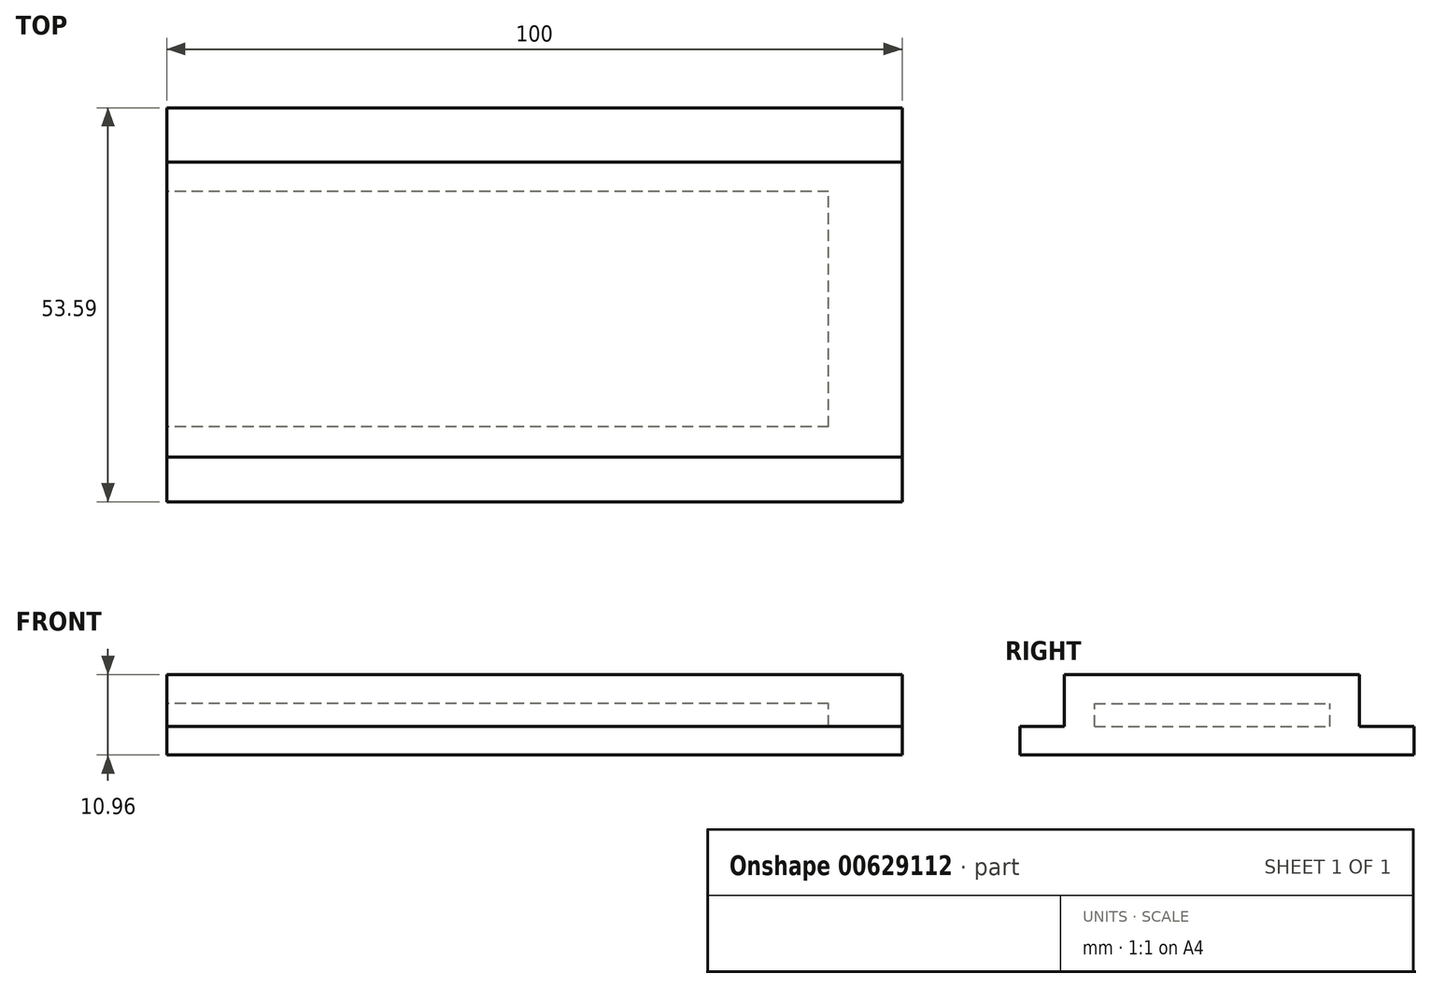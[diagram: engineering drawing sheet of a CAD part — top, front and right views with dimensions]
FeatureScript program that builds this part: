
annotation { "Feature Type Name" : "Feature", "Feature Type Description" : "" }
export const myFeature = defineFeature(function(context is Context, id is Id, definition is map)
    precondition{}
    {
        {
            var Q0;
            Q0=qCreatedBy(makeId("Right.planeOp"),FACE);
            var sketch = newSketch(context, id + "F0", { "sketchPlane" : qUnion([Q0])});
            skLineSegment(sketch, "E0", {"start": v(0, 0) * mm, "end": v(-24.54, 0) * mm});
            skLineSegment(sketch, "E1", {"start": v(-24.54, 0) * mm, "end": v(-24.54, 3.92) * mm});
            skLineSegment(sketch, "E2", {"start": v(-24.54, 3.92) * mm, "end": v(-18.5, 3.92) * mm});
            skLineSegment(sketch, "E3", {"start": v(-18.5, 3.92) * mm, "end": v(-18.5, 10.96) * mm});
            skLineSegment(sketch, "E4", {"start": v(-18.5, 10.96) * mm, "end": v(21.64, 10.96) * mm});
            skLineSegment(sketch, "E5", {"start": v(21.64, 10.96) * mm, "end": v(21.64, 3.92) * mm});
            skLineSegment(sketch, "E6", {"start": v(21.64, 3.92) * mm, "end": v(29.05, 3.92) * mm});
            skLineSegment(sketch, "E7", {"start": v(29.05, 3.92) * mm, "end": v(29.05, 0) * mm});
            skLineSegment(sketch, "E8", {"start": v(29.05, 0) * mm, "end": v(0, 0) * mm});
            skLineSegment(sketch, "E9.bottom", {"start": v(-14.37, 3.9) * mm, "end": v(17.63, 3.9) * mm});
            skLineSegment(sketch, "E9.top", {"start": v(-14.37, 7) * mm, "end": v(17.63, 7) * mm});
            skLineSegment(sketch, "E9.left", {"start": v(-14.37, 3.9) * mm, "end": v(-14.37, 7) * mm});
            skLineSegment(sketch, "E9.right", {"start": v(17.63, 3.9) * mm, "end": v(17.63, 7) * mm});
            skSolve(sketch);
        }
        {
            var Q0;
            Q0=makeQuery(id+"F0.imprint","IMPRINT",FACE,{"disambiguationData":[TD([[makeQuery(id+"F0.imprint","IMPRINT",EDGE,{"derivedFrom":sQuery(id+"F0.wireOp",EDGE,"E0")}),-1.0]])]});
            var Q1;
            Q1=makeQuery(id+"F0.imprint","IMPRINT",FACE,{"disambiguationData":[TD([[makeQuery(id+"F0.imprint","IMPRINT",EDGE,{"derivedFrom":sQuery(id+"F0.wireOp",EDGE,"E9.bottom")}),1.0]])]});
            extrude(context, id + "F1", {"entities" : qUnion([Q0, Q1]), "depth" : 100 * mm, "offsetDistance" : 25 * mm});
        }
        {
            var Q0;
            Q0=makeQuery(id+"F0.imprint","IMPRINT",FACE,{"disambiguationData":[TD([[makeQuery(id+"F0.imprint","IMPRINT",EDGE,{"derivedFrom":sQuery(id+"F0.wireOp",EDGE,"E9.bottom")}),1.0]])]});
            var Q1;
            Q1=makeQuery(id+"F1.opExtrude","CAP_FACE",FACE,{"disambiguationData":[OSD([sQuery(id+"F0.wireOp",EDGE,"E0"),sQuery(id+"F0.wireOp",EDGE,"E1"),sQuery(id+"F0.wireOp",EDGE,"E2"),sQuery(id+"F0.wireOp",EDGE,"E3"),sQuery(id+"F0.wireOp",EDGE,"E4"),sQuery(id+"F0.wireOp",EDGE,"E5"),sQuery(id+"F0.wireOp",EDGE,"E6"),sQuery(id+"F0.wireOp",EDGE,"E7"),sQuery(id+"F0.wireOp",EDGE,"E8")])],"isStart":false});
            extrude(context, id + "F2", {"entities" : qUnion([Q0]), "operationType" : NewBodyOperationType.REMOVE, "endBound" : BoundingType.UP_TO_SURFACE, "depth" : 25 * mm, "endBoundEntityFace" : qUnion([Q1]), "hasOffset" : true, "offsetDistance" : 10 * mm});
        }
    });
